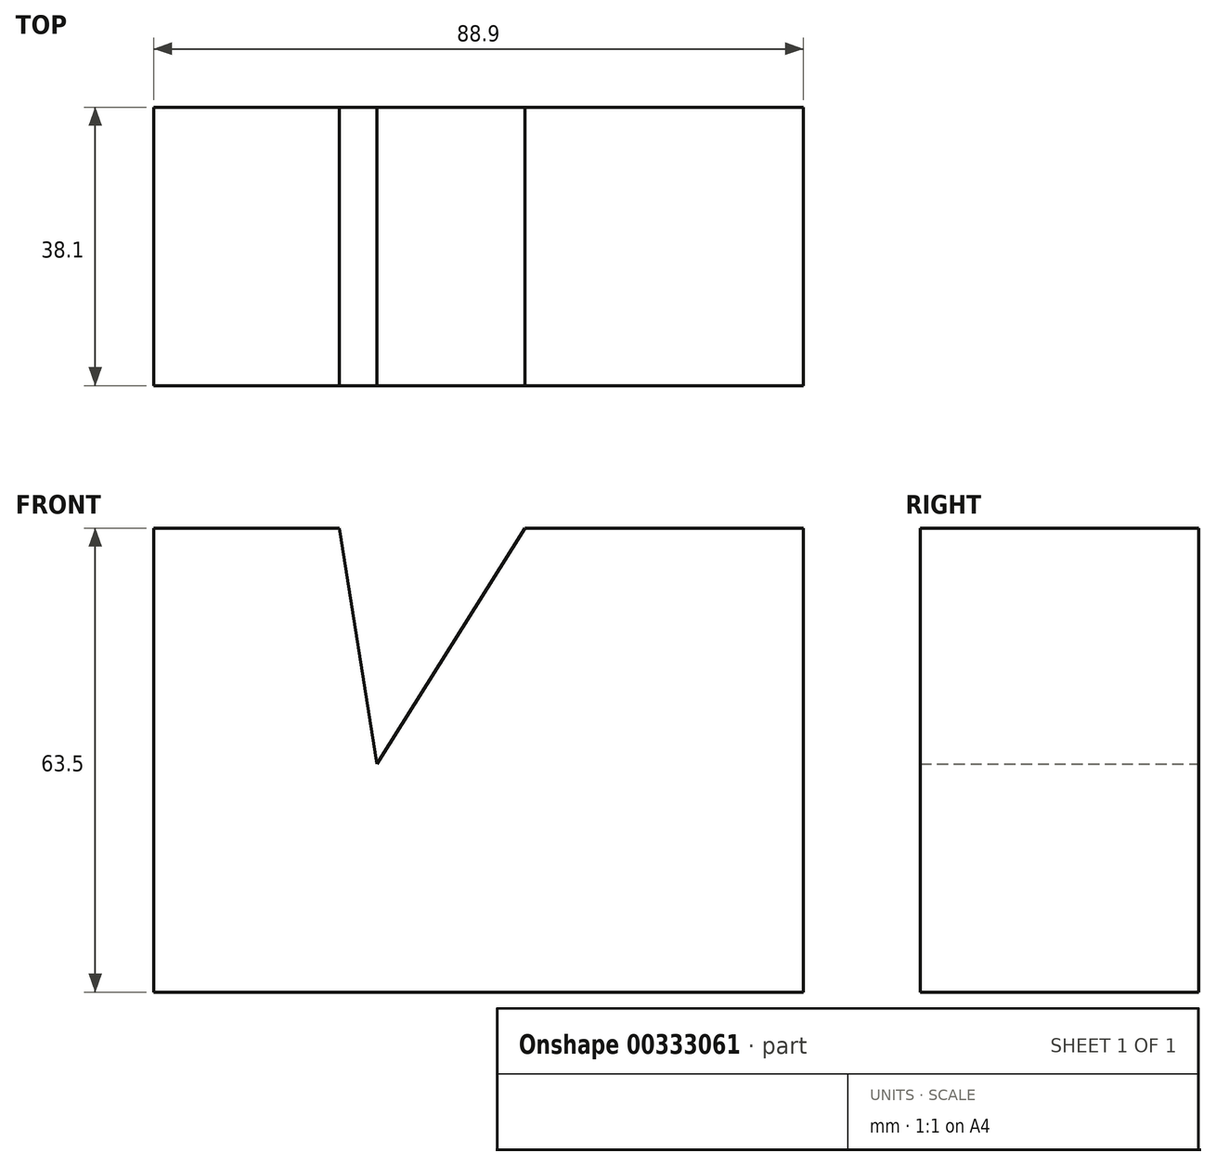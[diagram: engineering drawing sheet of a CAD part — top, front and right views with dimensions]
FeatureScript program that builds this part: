
annotation { "Feature Type Name" : "Feature", "Feature Type Description" : "" }
export const myFeature = defineFeature(function(context is Context, id is Id, definition is map)
    precondition{}
    {
        {
            var Q0;
            Q0=qCreatedBy(makeId("Front.planeOp"),FACE);
            var sketch = newSketch(context, id + "F0", { "sketchPlane" : qUnion([Q0])});
            skLineSegment(sketch, "E0", {"start": v(-54.05, -28.63) * mm, "end": v(34.85, -28.63) * mm});
            skLineSegment(sketch, "E1", {"start": v(-54.05, -28.63) * mm, "end": v(-54.05, 34.87) * mm});
            skLineSegment(sketch, "E2", {"start": v(-54.05, 34.87) * mm, "end": v(-28.65, 34.87) * mm});
            skLineSegment(sketch, "E3", {"start": v(34.85, -28.63) * mm, "end": v(34.85, 34.87) * mm});
            skLineSegment(sketch, "E4", {"start": v(34.85, 34.87) * mm, "end": v(-3.25, 34.87) * mm});
            skLineSegment(sketch, "E5", {"start": v(-28.65, 34.87) * mm, "end": v(-23.5, 2.6) * mm});
            skLineSegment(sketch, "E6", {"start": v(-23.5, 2.6) * mm, "end": v(-3.25, 34.87) * mm});
            skSolve(sketch);
        }
        {
            var Q0;
            Q0 = qSketchRegion(id + "F0", true);
            extrude(context, id + "F1", {"entities" : qUnion([Q0]), "depth" : 38.1 * mm});
        }
    });
